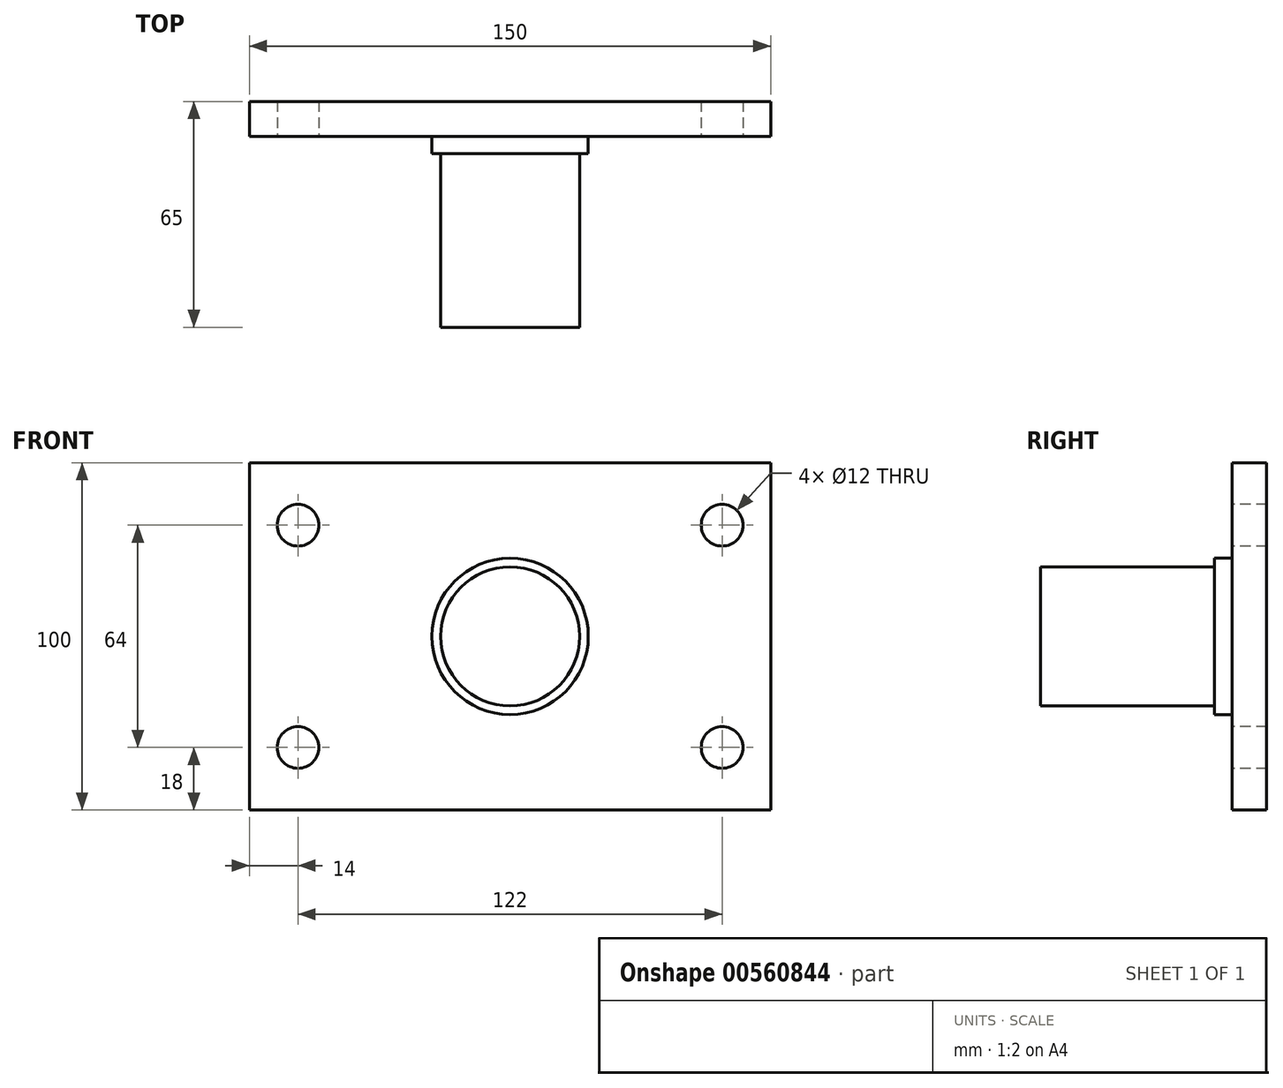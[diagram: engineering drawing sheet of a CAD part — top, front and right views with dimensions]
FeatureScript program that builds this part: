
annotation { "Feature Type Name" : "Feature", "Feature Type Description" : "" }
export const myFeature = defineFeature(function(context is Context, id is Id, definition is map)
    precondition{}
    {
        {
            var Q0;
            Q0=qCreatedBy(makeId("Front.planeOp"),FACE);
            var sketch = newSketch(context, id + "F0", { "sketchPlane" : qUnion([Q0])});
            skLineSegment(sketch, "E0.bottom", {"start": v(0, 0) * mm, "end": v(150, 0) * mm});
            skLineSegment(sketch, "E0.top", {"start": v(0, -100) * mm, "end": v(150, -100) * mm});
            skLineSegment(sketch, "E0.left", {"start": v(0, 0) * mm, "end": v(0, -100) * mm});
            skLineSegment(sketch, "E0.right", {"start": v(150, 0) * mm, "end": v(150, -100) * mm});
            skSolve(sketch);
        }
        {
            var Q0;
            Q0 = qSketchRegion(id + "F0", true);
            extrude(context, id + "F1", {"entities" : qUnion([Q0]), "depth" : 10 * mm, "offsetDistance" : 25 * mm});
        }
        {
            var Q0;
            Q0=makeQuery(id+"F1.opExtrude","CAP_FACE",FACE,{"disambiguationData":[OSD([sQuery(id+"F0.wireOp",EDGE,"E0.bottom"),sQuery(id+"F0.wireOp",EDGE,"E0.top"),sQuery(id+"F0.wireOp",EDGE,"E0.left"),sQuery(id+"F0.wireOp",EDGE,"E0.right")])],"isStart":false});
            var sketch = newSketch(context, id + "F2", { "sketchPlane" : qUnion([Q0])});
            skCircle(sketch, "E1", {"center": v(75, -50) * mm, "radius": 22.5 * mm});
            skPoint(sketch, "E1.centerSnap0", {"position": v(0, -50) * mm});
            skPoint(sketch, "E1.centerSnap1", {"position": v(75, 0) * mm});
            skSolve(sketch);
        }
        {
            var Q0;
            Q0 = qSketchRegion(id + "F2", true);
            extrude(context, id + "F3", {"entities" : qUnion([Q0]), "operationType" : NewBodyOperationType.ADD, "depth" : 5 * mm, "offsetDistance" : 25 * mm});
        }
        {
            var Q0;
            Q0=makeQuery(id+"F3.opExtrude","CAP_FACE",FACE,{"disambiguationData":[OSD([sQuery(id+"F2.wireOp",EDGE,"E1")])],"isStart":false});
            var sketch = newSketch(context, id + "F4", { "sketchPlane" : qUnion([Q0])});
            skCircle(sketch, "E2", {"center": v(75, -50) * mm, "radius": 20 * mm});
            skSolve(sketch);
        }
        {
            var Q0;
            Q0 = qSketchRegion(id + "F4", true);
            extrude(context, id + "F5", {"entities" : qUnion([Q0]), "operationType" : NewBodyOperationType.ADD, "depth" : 50 * mm, "offsetDistance" : 25 * mm});
        }
        {
            var Q0;
            Q0=makeQuery(id+"F1.opExtrude","CAP_FACE",FACE,{"disambiguationData":[OSD([sQuery(id+"F0.wireOp",EDGE,"E0.bottom"),sQuery(id+"F0.wireOp",EDGE,"E0.top"),sQuery(id+"F0.wireOp",EDGE,"E0.left"),sQuery(id+"F0.wireOp",EDGE,"E0.right")])],"isStart":false});
            var sketch = newSketch(context, id + "F6", { "sketchPlane" : qUnion([Q0])});
            skCircle(sketch, "E3", {"center": v(136, -18) * mm, "radius": 6 * mm});
            skSolve(sketch);
        }
        {
            var Q0;
            Q0=makeQuery(id+"F6.imprint","IMPRINT",FACE,{"disambiguationData":[TD([[makeQuery(id+"F6.imprint","IMPRINT",EDGE,{"derivedFrom":sQuery(id+"F6.wireOp",EDGE,"E3")}),-1.0]])]});
            var sketch = newSketch(context, id + "F7", { "sketchPlane" : qUnion([Q0])});
            skCircle(sketch, "E4", {"center": v(136, -82) * mm, "radius": 6 * mm});
            skSolve(sketch);
        }
        {
            var Q0;
            Q0=sQuery(id+"F6.wireOp",VERTEX,"E3.center");
            var Q1;
            Q1=makeQuery(id+"F1.opExtrude","SWEPT_BODY",BODY,{"disambiguationData":[OSD([sQuery(id+"F0.wireOp",EDGE,"E0.bottom"),sQuery(id+"F0.wireOp",EDGE,"E0.top"),sQuery(id+"F0.wireOp",EDGE,"E0.left"),sQuery(id+"F0.wireOp",EDGE,"E0.right")])]});
            hole(context, id + "F8", {"style" : HoleStyle.SIMPLE, "endStyle" : HoleEndStyle.THROUGH, "holeDiameter" : 12 * mm, "isTappedThrough" : true, "tappedDepth" : 12 * mm, "tapClearance" : 3, "locations" : qUnion([Q0]), "scope" : qUnion([Q1])});
        }
        {
            var Q0;
            Q0=sQuery(id+"F7.wireOp",VERTEX,"E4.center");
            var Q1;
            Q1=makeQuery(id+"F1.opExtrude","SWEPT_BODY",BODY,{"disambiguationData":[OSD([sQuery(id+"F0.wireOp",EDGE,"E0.bottom"),sQuery(id+"F0.wireOp",EDGE,"E0.top"),sQuery(id+"F0.wireOp",EDGE,"E0.left"),sQuery(id+"F0.wireOp",EDGE,"E0.right")])]});
            hole(context, id + "F9", {"style" : HoleStyle.SIMPLE, "endStyle" : HoleEndStyle.THROUGH, "holeDiameter" : 12 * mm, "isTappedThrough" : true, "tappedDepth" : 12 * mm, "tapClearance" : 3, "locations" : qUnion([Q0]), "scope" : qUnion([Q1])});
        }
        {
            var Q0;
            Q0=makeQuery(id+"F1.opExtrude","CAP_FACE",FACE,{"disambiguationData":[OSD([sQuery(id+"F0.wireOp",EDGE,"E0.bottom"),sQuery(id+"F0.wireOp",EDGE,"E0.top"),sQuery(id+"F0.wireOp",EDGE,"E0.left"),sQuery(id+"F0.wireOp",EDGE,"E0.right")])],"isStart":false});
            var sketch = newSketch(context, id + "F10", { "sketchPlane" : qUnion([Q0])});
            skCircle(sketch, "E5", {"center": v(14, -18) * mm, "radius": 6 * mm});
            skCircle(sketch, "E6", {"center": v(14, -82) * mm, "radius": 6 * mm});
            skSolve(sketch);
        }
        {
            var Q0;
            Q0=sQuery(id+"F10.wireOp",VERTEX,"E6.center");
            var Q1;
            Q1=sQuery(id+"F10.wireOp",VERTEX,"E5.center");
            var Q2;
            Q2=makeQuery(id+"F1.opExtrude","SWEPT_BODY",BODY,{"disambiguationData":[OSD([sQuery(id+"F0.wireOp",EDGE,"E0.bottom"),sQuery(id+"F0.wireOp",EDGE,"E0.top"),sQuery(id+"F0.wireOp",EDGE,"E0.left"),sQuery(id+"F0.wireOp",EDGE,"E0.right")])]});
            hole(context, id + "F11", {"style" : HoleStyle.SIMPLE, "endStyle" : HoleEndStyle.THROUGH, "holeDiameter" : 12 * mm, "isTappedThrough" : true, "tappedDepth" : 12 * mm, "tapClearance" : 3, "locations" : qUnion([Q0, Q1]), "scope" : qUnion([Q2])});
        }
    });
